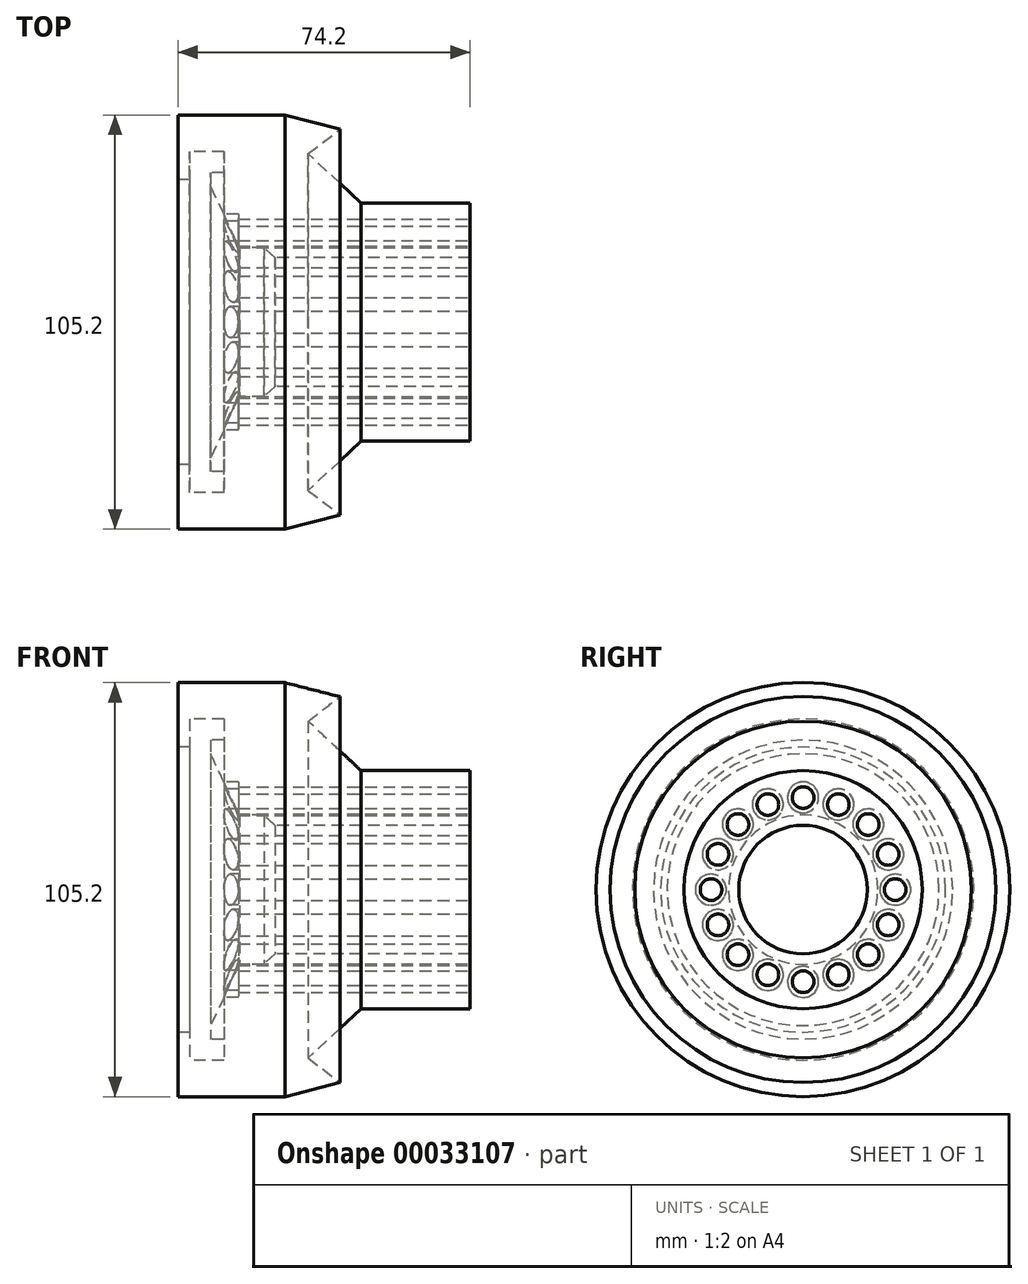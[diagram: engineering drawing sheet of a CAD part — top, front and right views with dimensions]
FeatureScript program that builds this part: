
annotation { "Feature Type Name" : "Feature", "Feature Type Description" : "" }
export const myFeature = defineFeature(function(context is Context, id is Id, definition is map)
    precondition{}
    {
        {
            var Q0;
            Q0=qCreatedBy(makeId("Front.planeOp"),FACE);
            var sketch = newSketch(context, id + "F0", { "sketchPlane" : qUnion([Q0])});
            skLineSegment(sketch, "E0", {"start": v(-46.49, 0) * mm, "end": v(-46.49, 52.6) * mm});
            skLineSegment(sketch, "E1", {"start": v(-46.49, 52.6) * mm, "end": v(-19.37, 52.6) * mm});
            skLineSegment(sketch, "E2", {"start": v(-19.37, 52.6) * mm, "end": v(-5.36, 49.02) * mm});
            skLineSegment(sketch, "E3", {"start": v(-5.36, 49.02) * mm, "end": v(-13.4, 42.76) * mm});
            skLineSegment(sketch, "E4", {"start": v(-13.4, 42.76) * mm, "end": v(0, 30.25) * mm});
            skLineSegment(sketch, "E5", {"start": v(0, 30.25) * mm, "end": v(27.71, 30.25) * mm});
            skLineSegment(sketch, "E6", {"start": v(27.71, 30.25) * mm, "end": v(27.71, 0) * mm});
            skLineSegment(sketch, "E7", {"start": v(-46.49, 0) * mm, "end": v(27.71, 0) * mm});
            skSolve(sketch);
        }
        {
            var Q0;
            Q0 = qSketchRegion(id + "F0", true);
            var Q1;
            Q1=sQuery(id+"F0.wireOp",EDGE,"E7");
            revolve(context, id + "F1", {"entities" : qUnion([Q0]), "axis" : qUnion([Q1]), "revolveType" : RevolveType.FULL});
        }
        {
            var Q0;
            Q0=qCreatedBy(makeId("Front.planeOp"),FACE);
            var sketch = newSketch(context, id + "F2", { "sketchPlane" : qUnion([Q0])});
            skLineSegment(sketch, "E8", {"start": v(-46.78, 0) * mm, "end": v(-46.78, 36.2) * mm});
            skLineSegment(sketch, "E9", {"start": v(-46.78, 36.2) * mm, "end": v(-43.5, 36.2) * mm});
            skLineSegment(sketch, "E10", {"start": v(-43.5, 36.2) * mm, "end": v(-43.5, 43.36) * mm});
            skLineSegment(sketch, "E11", {"start": v(-43.5, 43.36) * mm, "end": v(-34.86, 43.36) * mm});
            skLineSegment(sketch, "E12", {"start": v(-34.86, 43.36) * mm, "end": v(-34.86, 38) * mm});
            skLineSegment(sketch, "E13", {"start": v(-38.22, 38) * mm, "end": v(-38.22, 34.54) * mm});
            skLineSegment(sketch, "E14", {"start": v(-30.9, 18.96) * mm, "end": v(-24.7, 18.96) * mm});
            skLineSegment(sketch, "E15", {"start": v(-24.7, 18.96) * mm, "end": v(-21.89, 16.33) * mm});
            skLineSegment(sketch, "E16", {"start": v(-21.89, 16.33) * mm, "end": v(29.87, 16.33) * mm});
            skLineSegment(sketch, "E17", {"start": v(29.87, 16.33) * mm, "end": v(29.87, 0) * mm});
            skLineSegment(sketch, "E18", {"start": v(29.87, 0) * mm, "end": v(-46.78, 0) * mm});
            skLineSegment(sketch, "E19", {"start": v(-38.22, 38) * mm, "end": v(-34.86, 38) * mm});
            skLineSegment(sketch, "E20", {"start": v(-38.22, 34.54) * mm, "end": v(-30.9, 18.96) * mm});
            skSolve(sketch);
        }
        {
            var Q0;
            Q0 = qSketchRegion(id + "F2", true);
            var Q1;
            Q1=sQuery(id+"F2.wireOp",EDGE,"E18");
            revolve(context, id + "F3", {"operationType" : NewBodyOperationType.REMOVE, "entities" : qUnion([Q0]), "axis" : qUnion([Q1]), "revolveType" : RevolveType.FULL, "oppositeDirection" : true});
        }
        {
            var Q0;
            Q0=makeQuery(id+"F1.opRevolve","SWEPT_FACE",FACE,{"disambiguationData":[OSD([sQuery(id+"F0.wireOp",EDGE,"E6")])]});
            var sketch = newSketch(context, id + "F4", { "sketchPlane" : qUnion([Q0])});
            skCircle(sketch, "E21", {"center": v(0, 0) * mm, "radius": 23.4 * mm, "construction": true});
            skLineSegment(sketch, "E22", {"start": v(0, 0) * mm, "end": v(0, 30.25) * mm, "construction": true});
            skCircle(sketch, "E23", {"center": v(0, 23.4) * mm, "radius": 2.75 * mm});
            skCircle(sketch, "E24.1.0", {"center": v(-8.95, 21.61) * mm, "radius": 2.75 * mm});
            skCircle(sketch, "E24.2.0", {"center": v(-16.54, 16.54) * mm, "radius": 2.75 * mm});
            skCircle(sketch, "E24.3.0", {"center": v(-21.61, 8.95) * mm, "radius": 2.75 * mm});
            skCircle(sketch, "E24.4.0", {"center": v(-23.4, 0) * mm, "radius": 2.75 * mm});
            skCircle(sketch, "E24.5.0", {"center": v(-21.61, -8.95) * mm, "radius": 2.75 * mm});
            skCircle(sketch, "E24.6.0", {"center": v(-16.54, -16.54) * mm, "radius": 2.75 * mm});
            skCircle(sketch, "E24.7.0", {"center": v(-8.95, -21.61) * mm, "radius": 2.75 * mm});
            skCircle(sketch, "E24.8.0", {"center": v(0, -23.4) * mm, "radius": 2.75 * mm});
            skCircle(sketch, "E24.9.0", {"center": v(8.95, -21.61) * mm, "radius": 2.75 * mm});
            skCircle(sketch, "E24.10.0", {"center": v(16.54, -16.54) * mm, "radius": 2.75 * mm});
            skCircle(sketch, "E24.11.0", {"center": v(21.61, -8.95) * mm, "radius": 2.75 * mm});
            skCircle(sketch, "E24.12.0", {"center": v(23.4, 0) * mm, "radius": 2.75 * mm});
            skCircle(sketch, "E24.13.0", {"center": v(21.61, 8.95) * mm, "radius": 2.75 * mm});
            skCircle(sketch, "E24.14.0", {"center": v(16.54, 16.54) * mm, "radius": 2.75 * mm});
            skCircle(sketch, "E24.15.0", {"center": v(8.95, 21.61) * mm, "radius": 2.75 * mm});
            skSolve(sketch);
        }
        {
            var Q0;
            Q0=makeQuery(id+"F4.imprint","IMPRINT",FACE,{"disambiguationData":[TD([[makeQuery(id+"F4.imprint","IMPRINT",EDGE,{"derivedFrom":sQuery(id+"F4.wireOp",EDGE,"E23")}),1.0]])]});
            var Q1;
            Q1=makeQuery(id+"F4.imprint","IMPRINT",FACE,{"disambiguationData":[TD([[makeQuery(id+"F4.imprint","IMPRINT",EDGE,{"derivedFrom":sQuery(id+"F4.wireOp",EDGE,"E24.1.0")}),1.0]])]});
            var Q2;
            Q2=makeQuery(id+"F4.imprint","IMPRINT",FACE,{"disambiguationData":[TD([[makeQuery(id+"F4.imprint","IMPRINT",EDGE,{"derivedFrom":sQuery(id+"F4.wireOp",EDGE,"E24.2.0")}),1.0]])]});
            var Q3;
            Q3=makeQuery(id+"F4.imprint","IMPRINT",FACE,{"disambiguationData":[TD([[makeQuery(id+"F4.imprint","IMPRINT",EDGE,{"derivedFrom":sQuery(id+"F4.wireOp",EDGE,"E24.3.0")}),1.0]])]});
            var Q4;
            Q4=makeQuery(id+"F4.imprint","IMPRINT",FACE,{"disambiguationData":[TD([[makeQuery(id+"F4.imprint","IMPRINT",EDGE,{"derivedFrom":sQuery(id+"F4.wireOp",EDGE,"E24.4.0")}),1.0]])]});
            var Q5;
            Q5=makeQuery(id+"F4.imprint","IMPRINT",FACE,{"disambiguationData":[TD([[makeQuery(id+"F4.imprint","IMPRINT",EDGE,{"derivedFrom":sQuery(id+"F4.wireOp",EDGE,"E24.5.0")}),1.0]])]});
            var Q6;
            Q6=makeQuery(id+"F4.imprint","IMPRINT",FACE,{"disambiguationData":[TD([[makeQuery(id+"F4.imprint","IMPRINT",EDGE,{"derivedFrom":sQuery(id+"F4.wireOp",EDGE,"E24.6.0")}),1.0]])]});
            var Q7;
            Q7=makeQuery(id+"F4.imprint","IMPRINT",FACE,{"disambiguationData":[TD([[makeQuery(id+"F4.imprint","IMPRINT",EDGE,{"derivedFrom":sQuery(id+"F4.wireOp",EDGE,"E24.7.0")}),1.0]])]});
            var Q8;
            Q8=makeQuery(id+"F4.imprint","IMPRINT",FACE,{"disambiguationData":[TD([[makeQuery(id+"F4.imprint","IMPRINT",EDGE,{"derivedFrom":sQuery(id+"F4.wireOp",EDGE,"E24.8.0")}),1.0]])]});
            var Q9;
            Q9=makeQuery(id+"F4.imprint","IMPRINT",FACE,{"disambiguationData":[TD([[makeQuery(id+"F4.imprint","IMPRINT",EDGE,{"derivedFrom":sQuery(id+"F4.wireOp",EDGE,"E24.9.0")}),1.0]])]});
            var Q10;
            Q10=makeQuery(id+"F4.imprint","IMPRINT",FACE,{"disambiguationData":[TD([[makeQuery(id+"F4.imprint","IMPRINT",EDGE,{"derivedFrom":sQuery(id+"F4.wireOp",EDGE,"E24.10.0")}),1.0]])]});
            var Q11;
            Q11=makeQuery(id+"F4.imprint","IMPRINT",FACE,{"disambiguationData":[TD([[makeQuery(id+"F4.imprint","IMPRINT",EDGE,{"derivedFrom":sQuery(id+"F4.wireOp",EDGE,"E24.11.0")}),1.0]])]});
            var Q12;
            Q12=makeQuery(id+"F4.imprint","IMPRINT",FACE,{"disambiguationData":[TD([[makeQuery(id+"F4.imprint","IMPRINT",EDGE,{"derivedFrom":sQuery(id+"F4.wireOp",EDGE,"E24.12.0")}),1.0]])]});
            var Q13;
            Q13=makeQuery(id+"F4.imprint","IMPRINT",FACE,{"disambiguationData":[TD([[makeQuery(id+"F4.imprint","IMPRINT",EDGE,{"derivedFrom":sQuery(id+"F4.wireOp",EDGE,"E24.13.0")}),1.0]])]});
            var Q14;
            Q14=makeQuery(id+"F4.imprint","IMPRINT",FACE,{"disambiguationData":[TD([[makeQuery(id+"F4.imprint","IMPRINT",EDGE,{"derivedFrom":sQuery(id+"F4.wireOp",EDGE,"E24.14.0")}),1.0]])]});
            var Q15;
            Q15=makeQuery(id+"F4.imprint","IMPRINT",FACE,{"disambiguationData":[TD([[makeQuery(id+"F4.imprint","IMPRINT",EDGE,{"derivedFrom":sQuery(id+"F4.wireOp",EDGE,"E24.15.0")}),1.0]])]});
            extrude(context, id + "F5", {"entities" : qUnion([Q0, Q1, Q2, Q3, Q4, Q5, Q6, Q7, Q8, Q9, Q10, Q11, Q12, Q13, Q14, Q15]), "operationType" : NewBodyOperationType.REMOVE, "oppositeDirection" : true, "depth" : 116.55 * mm});
        }
        {
            var Q0;
            Q0=makeQuery(id+"F1.opRevolve","SWEPT_FACE",FACE,{"disambiguationData":[OSD([sQuery(id+"F0.wireOp",EDGE,"E0")])]});
            var sketch = newSketch(context, id + "F6", { "sketchPlane" : qUnion([Q0])});
            skCircle(sketch, "E25", {"center": v(0, 0) * mm, "radius": 23.44 * mm, "construction": true});
            skLineSegment(sketch, "E26", {"start": v(0, 0) * mm, "end": v(0, 27.38) * mm, "construction": true});
            skCircle(sketch, "E27", {"center": v(0, 23.44) * mm, "radius": 3.94 * mm});
            skCircle(sketch, "E28.1.0", {"center": v(-8.97, 21.66) * mm, "radius": 3.94 * mm});
            skCircle(sketch, "E28.2.0", {"center": v(-16.58, 16.58) * mm, "radius": 3.94 * mm});
            skCircle(sketch, "E28.3.0", {"center": v(-21.66, 8.97) * mm, "radius": 3.94 * mm});
            skCircle(sketch, "E28.4.0", {"center": v(-23.44, 0) * mm, "radius": 3.94 * mm});
            skCircle(sketch, "E28.5.0", {"center": v(-21.66, -8.97) * mm, "radius": 3.94 * mm});
            skCircle(sketch, "E28.6.0", {"center": v(-16.58, -16.58) * mm, "radius": 3.94 * mm});
            skCircle(sketch, "E28.7.0", {"center": v(-8.97, -21.66) * mm, "radius": 3.94 * mm});
            skCircle(sketch, "E28.8.0", {"center": v(0, -23.44) * mm, "radius": 3.94 * mm});
            skCircle(sketch, "E28.9.0", {"center": v(8.97, -21.66) * mm, "radius": 3.94 * mm});
            skCircle(sketch, "E28.10.0", {"center": v(16.58, -16.58) * mm, "radius": 3.94 * mm});
            skCircle(sketch, "E28.11.0", {"center": v(21.66, -8.97) * mm, "radius": 3.94 * mm});
            skCircle(sketch, "E28.12.0", {"center": v(23.44, 0) * mm, "radius": 3.94 * mm});
            skCircle(sketch, "E28.13.0", {"center": v(21.66, 8.97) * mm, "radius": 3.94 * mm});
            skCircle(sketch, "E28.14.0", {"center": v(16.58, 16.58) * mm, "radius": 3.94 * mm});
            skCircle(sketch, "E28.15.0", {"center": v(8.97, 21.66) * mm, "radius": 3.94 * mm});
            skSolve(sketch);
        }
        {
            var Q0;
            Q0 = qSketchRegion(id + "F6", true);
            extrude(context, id + "F7", {"entities" : qUnion([Q0]), "operationType" : NewBodyOperationType.REMOVE, "oppositeDirection" : true, "depth" : 15.35 * mm});
        }
    });
